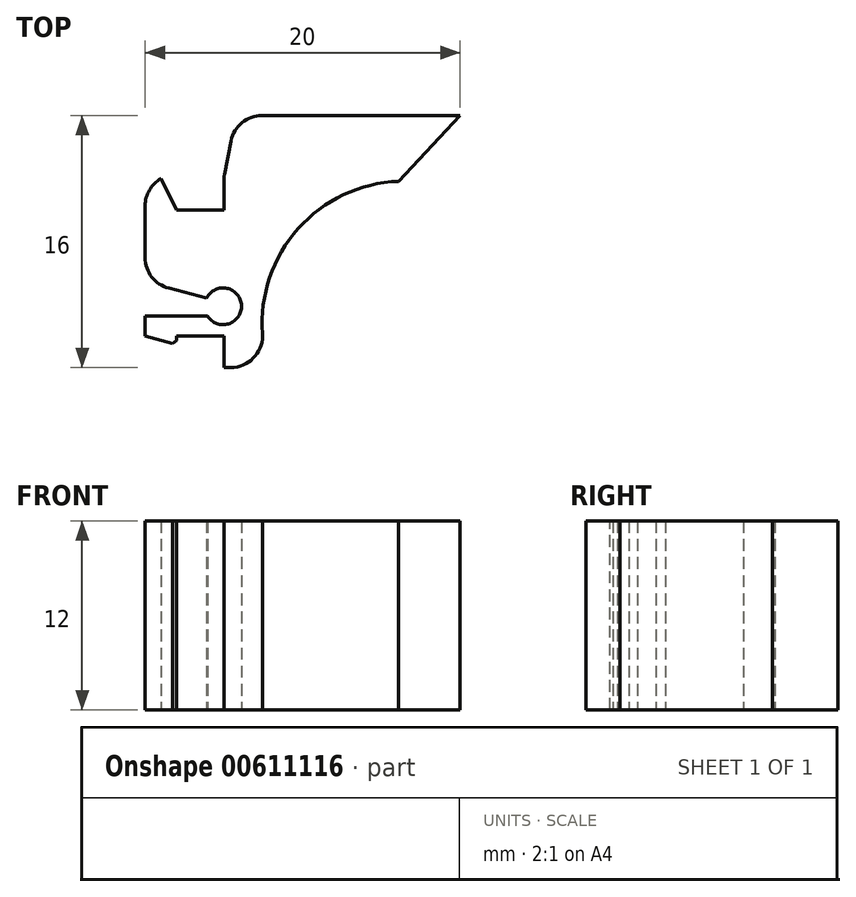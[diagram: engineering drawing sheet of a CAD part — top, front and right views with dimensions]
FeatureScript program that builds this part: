
annotation { "Feature Type Name" : "Feature", "Feature Type Description" : "" }
export const myFeature = defineFeature(function(context is Context, id is Id, definition is map)
    precondition{}
    {
        {
            var Q0;
            Q0=qCreatedBy(makeId("Top.planeOp"),FACE);
            var sketch = newSketch(context, id + "F0", { "sketchPlane" : qUnion([Q0])});
            skLineSegment(sketch, "E0", {"start": v(0, 15.06) * mm, "end": v(-3, 15.06) * mm});
            skLineSegment(sketch, "E1", {"start": v(-4, 17.06) * mm, "end": v(-5, 17.06) * mm});
            skLineSegment(sketch, "E2", {"start": v(-5, 17.06) * mm, "end": v(-5, 10.49) * mm});
            skLineSegment(sketch, "E3", {"start": v(-3, 7.06) * mm, "end": v(0, 7.06) * mm});
            skLineSegment(sketch, "E4", {"start": v(0, 7.06) * mm, "end": v(0, 5.06) * mm});
            skLineSegment(sketch, "E5", {"start": v(0, 15.06) * mm, "end": v(0, 17.14) * mm});
            skLineSegment(sketch, "E6", {"start": v(0.77, 21.06) * mm, "end": v(15, 21.06) * mm});
            skLineSegment(sketch, "E7", {"start": v(15, 21.06) * mm, "end": v(11.09, 16.89) * mm});
            skLineSegment(sketch, "E8", {"start": v(-3, 15.06) * mm, "end": v(-4, 17.06) * mm});
            skLineSegment(sketch, "E9", {"start": v(0, 17.14) * mm, "end": v(0.77, 21.06) * mm});
            skArc(sketch, "E10", {"start": v(11.09, 16.89) * mm, "mid": v(4.72, 13.88) * mm, "end": v(2.45, 7.21) * mm});
            skLineSegment(sketch, "E11", {"start": v(0, 5.06) * mm, "end": v(2.45, 5.06) * mm});
            skLineSegment(sketch, "E12", {"start": v(2.45, 5.06) * mm, "end": v(2.45, 7.21) * mm});
            skLineSegment(sketch, "E13", {"start": v(0.77, 21.06) * mm, "end": v(2.13, 21.06) * mm});
            skLineSegment(sketch, "E14", {"start": v(-5, 7.06) * mm, "end": v(-3, 6.52) * mm});
            skLineSegment(sketch, "E15", {"start": v(-3, 6.52) * mm, "end": v(-3, 7.06) * mm});
            skLineSegment(sketch, "E16.trimOffspring", {"start": v(-5, 7.64) * mm, "end": v(-5, 7.06) * mm});
            skLineSegment(sketch, "E17", {"start": v(-5, 7.64) * mm, "end": v(-5, 8.33) * mm});
            skLineSegment(sketch, "E18", {"start": v(-5, 8.33) * mm, "end": v(-1.04, 8.33) * mm});
            skArc(sketch, "E19", {"start": v(-1.04, 8.33) * mm, "mid": v(1.12, 9) * mm, "end": v(-1.09, 9.49) * mm});
            skPoint(sketch, "E20.orphan", {"position": v(0, 9.49) * mm});
            skLineSegment(sketch, "E21.trimOffspring", {"start": v(0, 8.33) * mm, "end": v(-0.1, 8.41) * mm});
            skPoint(sketch, "E22.start.orphan", {"position": v(0, 7.64) * mm});
            skLineSegment(sketch, "E23", {"start": v(-1.09, 9.49) * mm, "end": v(-5, 10.49) * mm});
            skSolve(sketch);
        }
        {
            var Q0;
            Q0 = qSketchRegion(id + "F0", true);
            extrude(context, id + "F1", {"entities" : qUnion([Q0]), "depth" : 12 * mm, "offsetDistance" : 25 * mm});
        }
        {
            var Q0;
            Q0=makeQuery(id+"F1.opExtrude","SWEPT_EDGE",EDGE,{"disambiguationData":[OSD([sQuery(id+"F0.wireOp",EDGE,"E11"),sQuery(id+"F0.wireOp",EDGE,"E12")])]});
            var Q1;
            Q1=makeQuery(id+"F1.opExtrude","SWEPT_EDGE",EDGE,{"disambiguationData":[OSD([sQuery(id+"F0.wireOp",EDGE,"E1"),sQuery(id+"F0.wireOp",EDGE,"E2")])]});
            var Q2;
            Q2=makeQuery(id+"F1.opExtrude","SWEPT_EDGE",EDGE,{"disambiguationData":[OSD([sQuery(id+"F0.wireOp",EDGE,"E2"),sQuery(id+"F0.wireOp",EDGE,"f3tIhAhF-3j2N-D4z8-o5FM-D4O2WV5zDnEJ")])]});
            var Q3;
            Q3=makeQuery(id+"F1.opExtrude","SWEPT_EDGE",EDGE,{"disambiguationData":[OSD([sQuery(id+"F0.wireOp",EDGE,"E9"),sQuery(id+"F0.wireOp",EDGE,"E13")])]});
            fillet(context, id + "F2", {"entities" : qUnion([Q0, Q1, Q2, Q3]), "radius" : 2 * mm, "tangentPropagation" : true, "allowEdgeOverflow" : false});
        }
        {
            var Q0;
            Q0=makeQuery(id+"F1.opExtrude","SWEPT_EDGE",EDGE,{"disambiguationData":[OSD([sQuery(id+"F0.wireOp",EDGE,"E14"),sQuery(id+"F0.wireOp",EDGE,"E15")])]});
            chamfer(context, id + "F3", {"entities" : qUnion([Q0]), "width" : .2 * mm, "tangentPropagation" : true});
        }
    });
